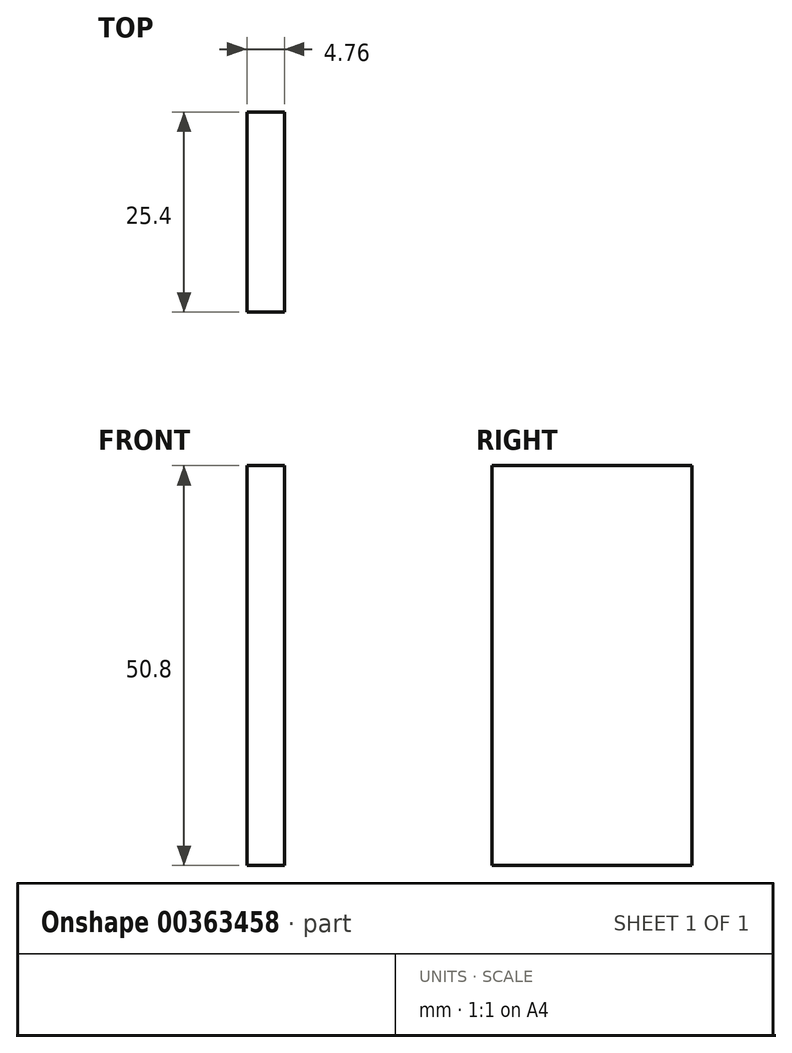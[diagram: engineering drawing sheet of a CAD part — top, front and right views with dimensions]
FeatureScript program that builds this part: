
annotation { "Feature Type Name" : "Feature", "Feature Type Description" : "" }
export const myFeature = defineFeature(function(context is Context, id is Id, definition is map)
    precondition{}
    {
        {
            var Q0;
            Q0=qCreatedBy(makeId("Right.planeOp"),FACE);
            var sketch = newSketch(context, id + "F0", { "sketchPlane" : qUnion([Q0])});
            skLineSegment(sketch, "E0.bottom", {"start": v(0, 0) * mm, "end": v(25.4, 0) * mm});
            skLineSegment(sketch, "E0.top", {"start": v(0, 50.8) * mm, "end": v(25.4, 50.8) * mm});
            skLineSegment(sketch, "E0.left", {"start": v(0, 0) * mm, "end": v(0, 50.8) * mm});
            skLineSegment(sketch, "E0.right", {"start": v(25.4, 0) * mm, "end": v(25.4, 50.8) * mm});
            skSolve(sketch);
        }
        {
            var Q0;
            Q0 = qSketchRegion(id + "F0", true);
            extrude(context, id + "F1", {"entities" : qUnion([Q0]), "depth" : 4.76 * mm});
        }
    });
